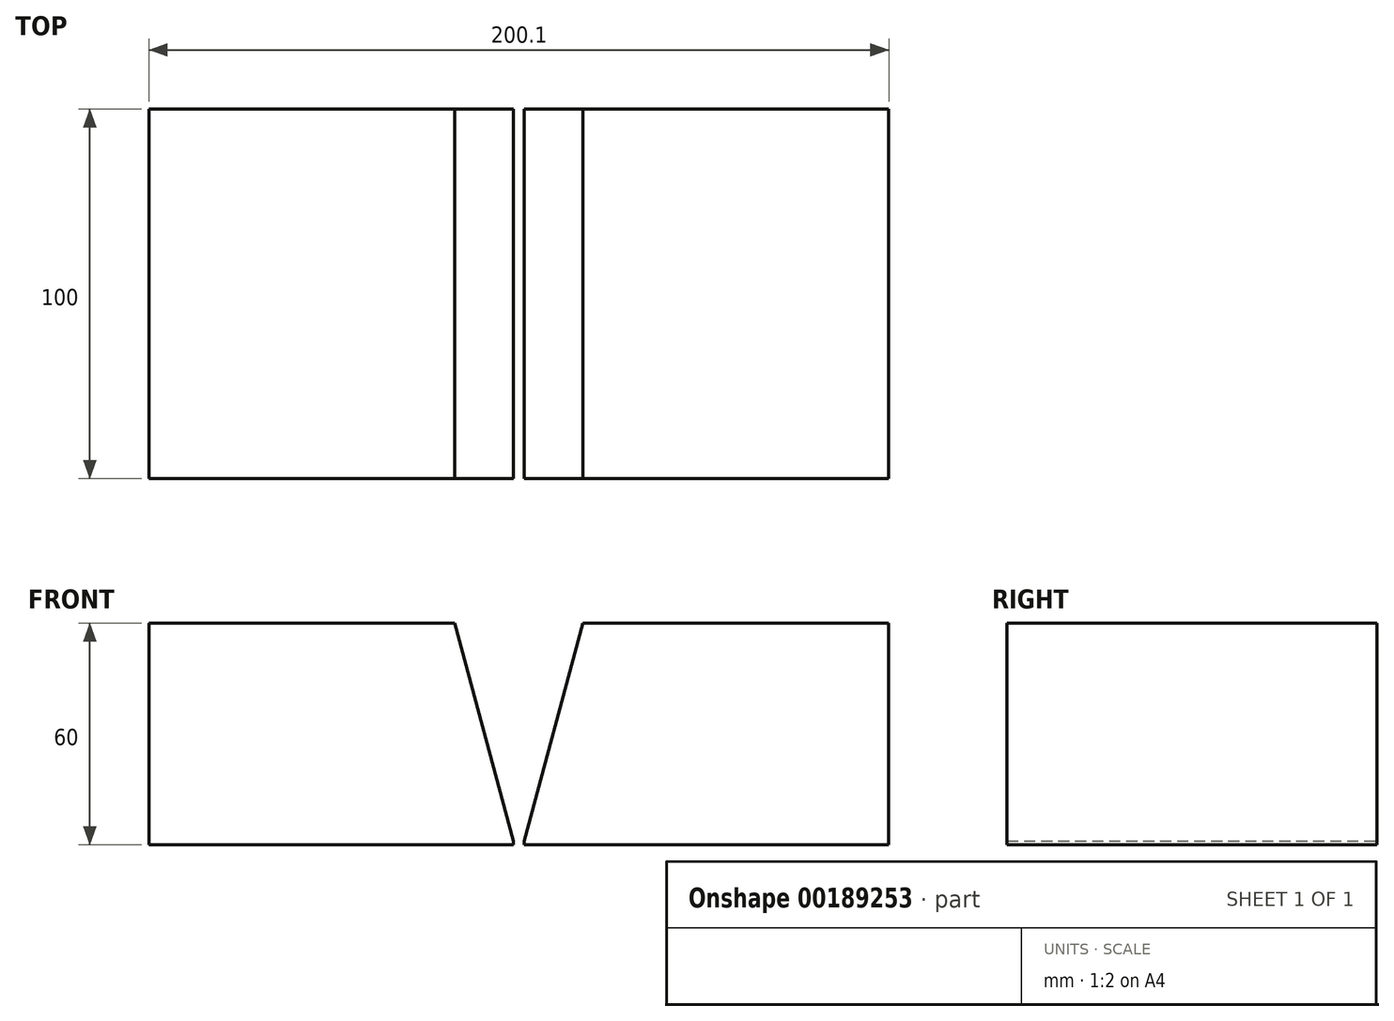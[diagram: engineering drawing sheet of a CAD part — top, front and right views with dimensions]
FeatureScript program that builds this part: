
annotation { "Feature Type Name" : "Feature", "Feature Type Description" : "" }
export const myFeature = defineFeature(function(context is Context, id is Id, definition is map)
    precondition{}
    {
        {
            var Q0;
            Q0=qCreatedBy(makeId("Front.planeOp"),FACE);
            var sketch = newSketch(context, id + "F0", { "sketchPlane" : qUnion([Q0])});
            skLineSegment(sketch, "E0", {"start": v(0, 35.15) * mm, "end": v(0, -34.81) * mm, "construction": true});
            skLineSegment(sketch, "E1", {"start": v(-1.5, 2) * mm, "end": v(-17.3, 61) * mm});
            skLineSegment(sketch, "E2", {"start": v(-17.3, 61) * mm, "end": v(-100.05, 61) * mm});
            skLineSegment(sketch, "E3", {"start": v(-100.05, 61) * mm, "end": v(-100.05, 1) * mm});
            skLineSegment(sketch, "E4.MirrorCS", {"start": v(100.05, 61) * mm, "end": v(100.05, 1) * mm});
            skLineSegment(sketch, "E5.MirrorCS", {"start": v(17.3, 61) * mm, "end": v(100.05, 61) * mm});
            skLineSegment(sketch, "E6.MirrorCS", {"start": v(100.05, 1) * mm, "end": v(1.5, 1) * mm});
            skLineSegment(sketch, "E7.MirrorCS", {"start": v(1.5, 2) * mm, "end": v(17.3, 61) * mm});
            skLineSegment(sketch, "E8", {"start": v(-1.5, 1) * mm, "end": v(-1.5, 2) * mm});
            skLineSegment(sketch, "E9", {"start": v(1.5, 2) * mm, "end": v(1.5, 1) * mm});
            skLineSegment(sketch, "E10", {"start": v(-100.05, 1) * mm, "end": v(-1.5, 1) * mm});
            skSolve(sketch);
        }
        {
            var Q0;
            Q0=makeQuery(id+"F0.imprint","IMPRINT",FACE,{"disambiguationData":[TD([[makeQuery(id+"F0.imprint","IMPRINT",EDGE,{"derivedFrom":sQuery(id+"F0.wireOp",EDGE,"E1")}),1.0]])]});
            var Q1;
            Q1=makeQuery(id+"F0.imprint","IMPRINT",FACE,{"disambiguationData":[TD([[makeQuery(id+"F0.imprint","IMPRINT",EDGE,{"derivedFrom":sQuery(id+"F0.wireOp",EDGE,"E4.MirrorCS")}),-1.0]])]});
            extrude(context, id + "F1", {"entities" : qUnion([Q0, Q1]), "depth" : 100 * mm});
        }
    });
